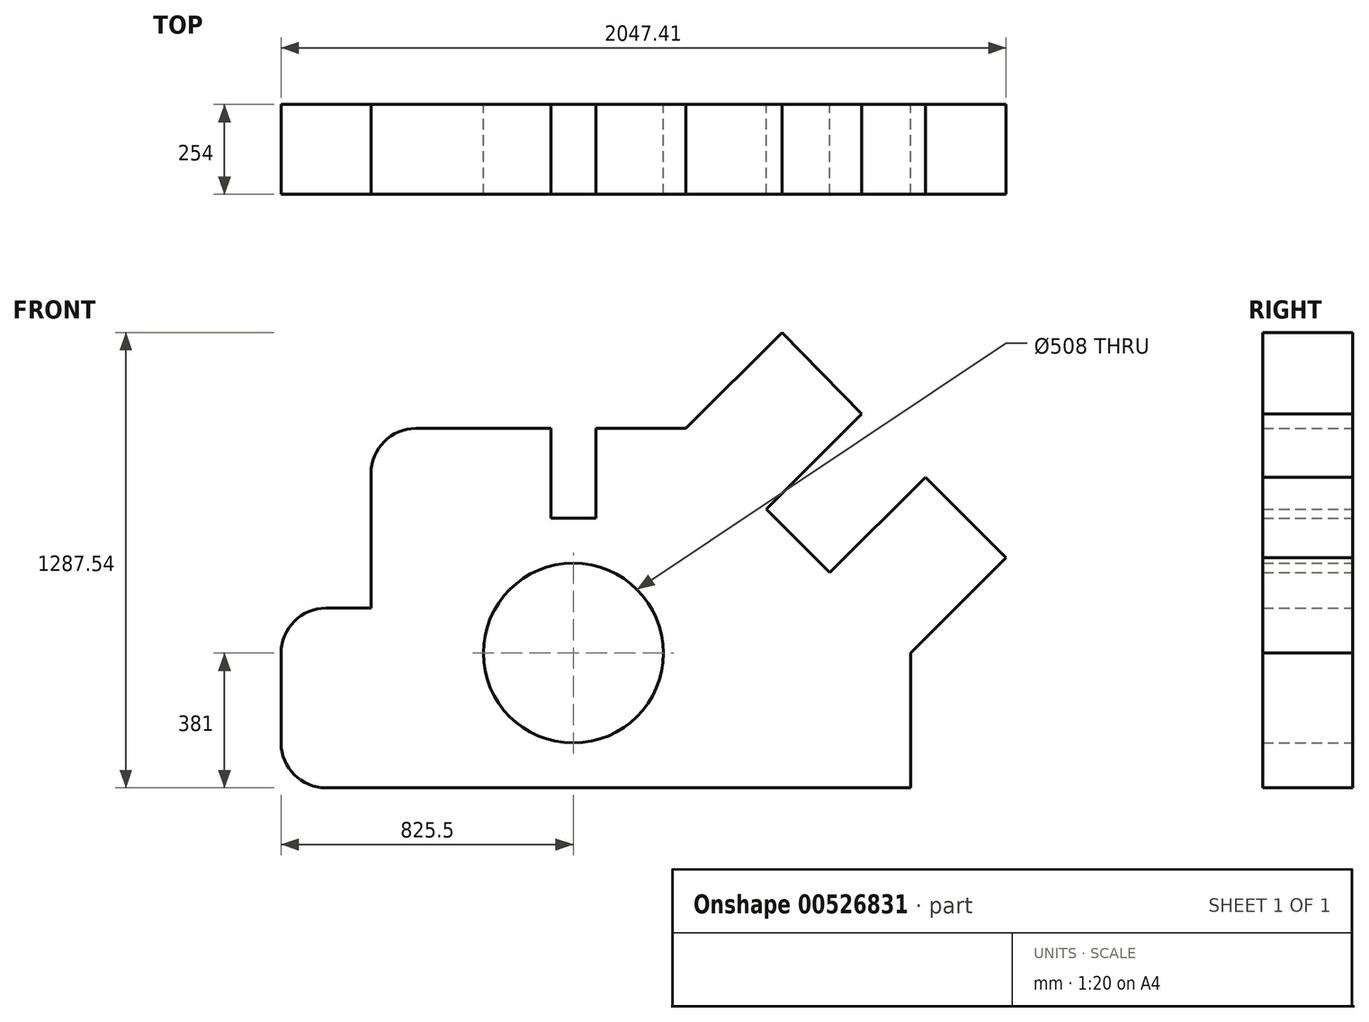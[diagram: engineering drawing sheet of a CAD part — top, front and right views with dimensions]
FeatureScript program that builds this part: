
annotation { "Feature Type Name" : "Feature", "Feature Type Description" : "" }
export const myFeature = defineFeature(function(context is Context, id is Id, definition is map)
    precondition{}
    {
        {
            var Q0;
            Q0=qCreatedBy(makeId("Front.planeOp"),FACE);
            var sketch = newSketch(context, id + "F0", { "sketchPlane" : qUnion([Q0])});
            skLineSegment(sketch, "E0", {"start": v(127, 0) * mm, "end": v(1778, 0) * mm});
            skLineSegment(sketch, "E1", {"start": v(1778, 0) * mm, "end": v(1778, 381) * mm});
            skLineSegment(sketch, "E2", {"start": v(0, 127) * mm, "end": v(0, 381) * mm});
            skPoint(sketch, "E3.visualSharp", {"position": v(0, 0) * mm});
            skArc(sketch, "E3.filletArc", {"start": v(0, 127) * mm, "mid": v(37.2, 37.2) * mm, "end": v(127, 0) * mm});
            skCircle(sketch, "E4", {"center": v(825.5, 381) * mm, "radius": 254 * mm});
            skLineSegment(sketch, "E5", {"start": v(127, 508) * mm, "end": v(254, 508) * mm});
            skLineSegment(sketch, "E6", {"start": v(254, 508) * mm, "end": v(254, 889) * mm});
            skLineSegment(sketch, "E7", {"start": v(381, 1016) * mm, "end": v(762, 1016) * mm});
            skLineSegment(sketch, "E8", {"start": v(762, 1016) * mm, "end": v(762, 762) * mm});
            skLineSegment(sketch, "E9", {"start": v(762, 762) * mm, "end": v(889, 762) * mm});
            skLineSegment(sketch, "E10", {"start": v(889, 762) * mm, "end": v(889, 1016) * mm});
            skLineSegment(sketch, "E11", {"start": v(889, 1016) * mm, "end": v(1143, 1016) * mm});
            skLineSegment(sketch, "E12", {"start": v(1778, 381) * mm, "end": v(2047.4, 650.4) * mm});
            skLineSegment(sketch, "E13", {"start": v(2047.4, 650.4) * mm, "end": v(1819.7, 878.11) * mm});
            skLineSegment(sketch, "E14", {"start": v(1819.7, 878.11) * mm, "end": v(1550.3, 608.7) * mm});
            skLineSegment(sketch, "E15", {"start": v(1550.3, 608.7) * mm, "end": v(1370.7, 788.3) * mm});
            skLineSegment(sketch, "E16", {"start": v(1370.7, 788.3) * mm, "end": v(1640.1, 1057.72) * mm});
            skLineSegment(sketch, "E17", {"start": v(1640.1, 1057.72) * mm, "end": v(1414.54, 1287.54) * mm});
            skLineSegment(sketch, "E18", {"start": v(1414.54, 1287.54) * mm, "end": v(1143, 1016) * mm});
            skPoint(sketch, "E19.visualSharp", {"position": v(254, 1016) * mm});
            skArc(sketch, "E19.filletArc", {"start": v(381, 1016) * mm, "mid": v(291.2, 978.8) * mm, "end": v(254, 889) * mm});
            skPoint(sketch, "E20.visualSharp", {"position": v(0, 508) * mm});
            skArc(sketch, "E20.filletArc", {"start": v(127, 508) * mm, "mid": v(37.2, 470.8) * mm, "end": v(0, 381) * mm});
            skSolve(sketch);
        }
        {
            var Q0;
            Q0=makeQuery(id+"F0.imprint","IMPRINT",FACE,{"disambiguationData":[TD([[makeQuery(id+"F0.imprint","IMPRINT",EDGE,{"derivedFrom":sQuery(id+"F0.wireOp",EDGE,"E0")}),1.0]])]});
            var Q1;
            Q1 = qConstructionFilter(qBodyType(qCreatedBy(id + "F0" ,EDGE), BodyType.WIRE), ConstructionObject.NO);
            extrude(context, id + "F1", {"entities" : qUnion([Q0]), "surfaceEntities" : qUnion([Q1]), "depth" : 254 * mm, "offsetDistance" : 25.4 * mm});
        }
    });
